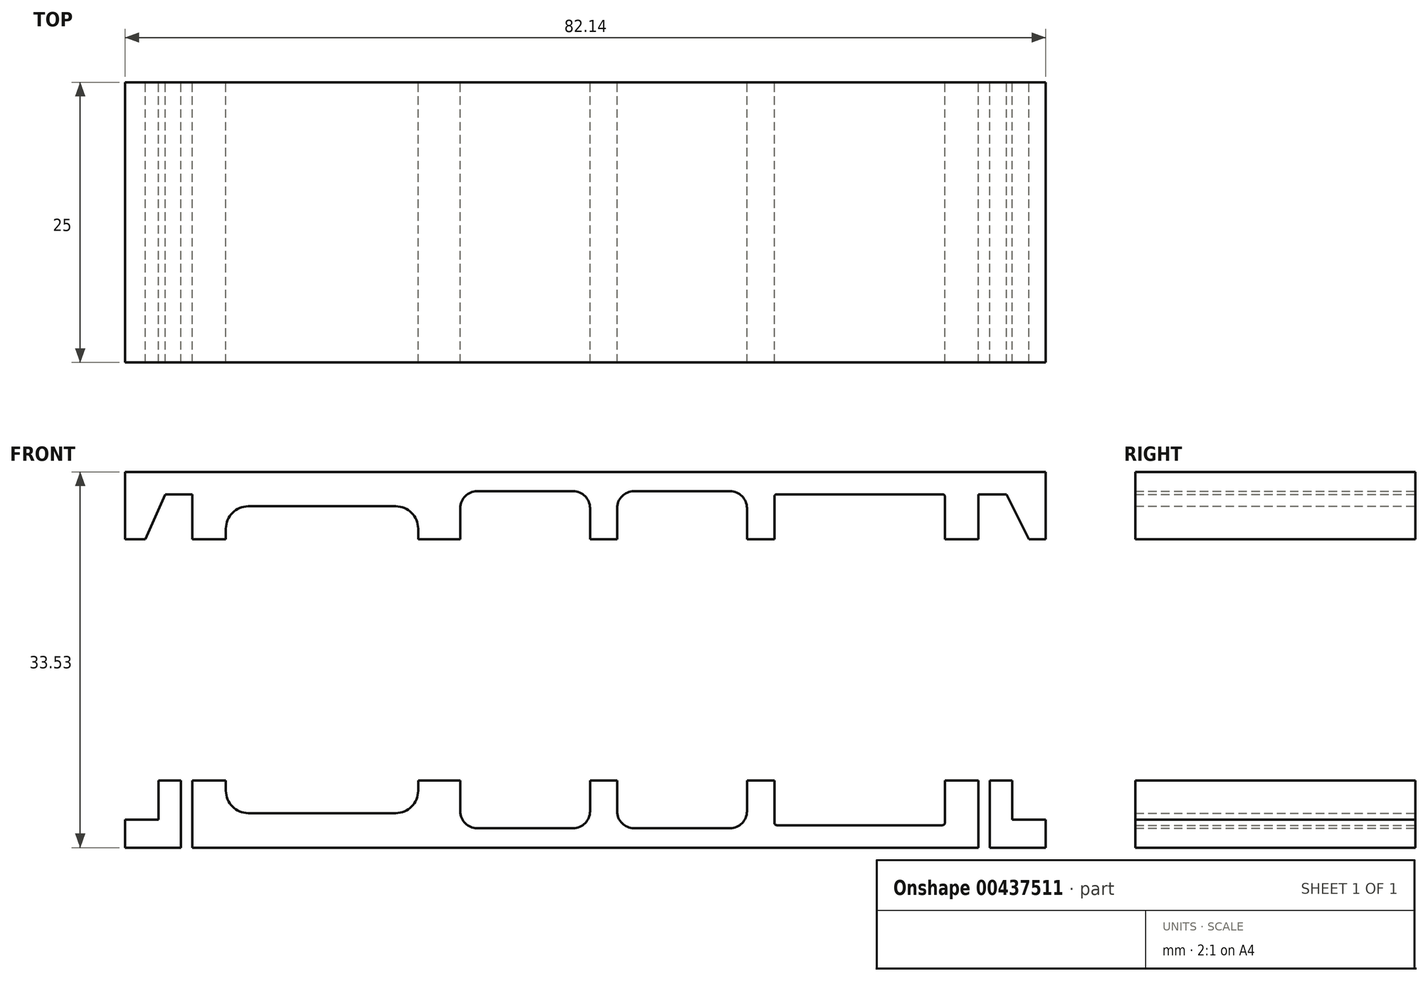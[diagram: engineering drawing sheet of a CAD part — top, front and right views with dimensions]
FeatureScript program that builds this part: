
annotation { "Feature Type Name" : "Feature", "Feature Type Description" : "" }
export const myFeature = defineFeature(function(context is Context, id is Id, definition is map)
    precondition{}
    {
        {
            var Q0;
            Q0=qCreatedBy(makeId("Front.planeOp"),FACE);
            var sketch = newSketch(context, id + "F0", { "sketchPlane" : qUnion([Q0])});
            skLineSegment(sketch, "E0.bottom", {"start": v(33.57, -6) * mm, "end": v(-33.57, -6) * mm});
            skLineSegment(sketch, "E0.top", {"start": v(33.57, 6) * mm, "end": v(-33.57, 6) * mm});
            skLineSegment(sketch, "E0.left", {"start": v(35.07, -4.5) * mm, "end": v(35.07, 4.5) * mm});
            skLineSegment(sketch, "E0.right", {"start": v(-35.07, -4.5) * mm, "end": v(-35.07, 4.5) * mm});
            skPoint(sketch, "E0.middle", {"position": v(0, 0) * mm});
            skLineSegment(sketch, "E1", {"start": v(-35.07, 0) * mm, "end": v(35.07, 0) * mm, "construction": true});
            skLineSegment(sketch, "E2.bottom", {"start": v(-16.92, -2.92) * mm, "end": v(-30.07, -2.92) * mm});
            skLineSegment(sketch, "E2.top", {"start": v(-16.92, 2.93) * mm, "end": v(-30.07, 2.93) * mm});
            skLineSegment(sketch, "E2.left", {"start": v(-14.92, -0.92) * mm, "end": v(-14.92, 0.93) * mm});
            skLineSegment(sketch, "E2.right", {"start": v(-32.07, -0.92) * mm, "end": v(-32.07, 0.93) * mm});
            skPoint(sketch, "E2.middle", {"position": v(-23.5, 0) * mm});
            skLineSegment(sketch, "E3.bottom", {"start": v(-1.09, 4.27) * mm, "end": v(-9.67, 4.27) * mm});
            skLineSegment(sketch, "E3.top", {"start": v(-1.09, -4.26) * mm, "end": v(-9.67, -4.26) * mm});
            skLineSegment(sketch, "E3.left", {"start": v(0.41, 2.77) * mm, "end": v(0.41, -2.76) * mm});
            skLineSegment(sketch, "E3.right", {"start": v(-11.17, 2.77) * mm, "end": v(-11.17, -2.76) * mm});
            skPoint(sketch, "E3.middle", {"position": v(-5.38, 0) * mm});
            skLineSegment(sketch, "E4.bottom", {"start": v(12.91, 4.27) * mm, "end": v(4.33, 4.27) * mm});
            skLineSegment(sketch, "E4.top", {"start": v(12.91, -4.26) * mm, "end": v(4.33, -4.26) * mm});
            skLineSegment(sketch, "E4.left", {"start": v(14.41, 2.77) * mm, "end": v(14.41, -2.76) * mm});
            skLineSegment(sketch, "E4.right", {"start": v(2.83, 2.77) * mm, "end": v(2.83, -2.76) * mm});
            skPoint(sketch, "E4.middle", {"position": v(8.62, 0) * mm});
            skLineSegment(sketch, "E5.bottom", {"start": v(31.87, -4) * mm, "end": v(17.07, -4) * mm});
            skLineSegment(sketch, "E5.top", {"start": v(31.87, 4) * mm, "end": v(17.07, 4) * mm});
            skLineSegment(sketch, "E5.left", {"start": v(32.07, -3.8) * mm, "end": v(32.07, 3.8) * mm});
            skLineSegment(sketch, "E5.right", {"start": v(16.87, -3.8) * mm, "end": v(16.87, 3.8) * mm});
            skPoint(sketch, "E5.middle", {"position": v(24.47, 0) * mm});
            skPoint(sketch, "E6.visualSharp", {"position": v(-32.07, 2.93) * mm});
            skArc(sketch, "E6.filletArc", {"start": v(-30.07, 2.93) * mm, "mid": v(-31.49, 2.34) * mm, "end": v(-32.07, 0.93) * mm});
            skPoint(sketch, "E7.visualSharp", {"position": v(-14.92, 2.93) * mm});
            skArc(sketch, "E7.filletArc", {"start": v(-14.92, 0.93) * mm, "mid": v(-15.5, 2.34) * mm, "end": v(-16.92, 2.93) * mm});
            skPoint(sketch, "E8.visualSharp", {"position": v(-14.92, -2.92) * mm});
            skArc(sketch, "E8.filletArc", {"start": v(-16.92, -2.92) * mm, "mid": v(-15.5, -2.34) * mm, "end": v(-14.92, -0.92) * mm});
            skPoint(sketch, "E9.visualSharp", {"position": v(-32.07, -2.93) * mm});
            skArc(sketch, "E9.filletArc", {"start": v(-32.07, -0.92) * mm, "mid": v(-31.49, -2.34) * mm, "end": v(-30.07, -2.92) * mm});
            skPoint(sketch, "E10.visualSharp", {"position": v(-11.17, 4.27) * mm});
            skArc(sketch, "E10.filletArc", {"start": v(-9.67, 4.27) * mm, "mid": v(-10.73, 3.83) * mm, "end": v(-11.17, 2.77) * mm});
            skPoint(sketch, "E11.visualSharp", {"position": v(0.41, 4.27) * mm});
            skArc(sketch, "E11.filletArc", {"start": v(0.41, 2.77) * mm, "mid": v(-0.03, 3.83) * mm, "end": v(-1.09, 4.27) * mm});
            skPoint(sketch, "E12.visualSharp", {"position": v(-11.17, -4.26) * mm});
            skArc(sketch, "E12.filletArc", {"start": v(-11.17, -2.76) * mm, "mid": v(-10.73, -3.83) * mm, "end": v(-9.67, -4.26) * mm});
            skPoint(sketch, "E13.visualSharp", {"position": v(0.41, -4.26) * mm});
            skArc(sketch, "E13.filletArc", {"start": v(-1.09, -4.26) * mm, "mid": v(-0.03, -3.83) * mm, "end": v(0.41, -2.76) * mm});
            skPoint(sketch, "E14.visualSharp", {"position": v(2.83, 4.26) * mm});
            skArc(sketch, "E14.filletArc", {"start": v(4.33, 4.26) * mm, "mid": v(3.27, 3.83) * mm, "end": v(2.83, 2.77) * mm});
            skPoint(sketch, "E15.visualSharp", {"position": v(14.41, 4.27) * mm});
            skArc(sketch, "E15.filletArc", {"start": v(14.41, 2.77) * mm, "mid": v(13.97, 3.83) * mm, "end": v(12.91, 4.27) * mm});
            skPoint(sketch, "E16.visualSharp", {"position": v(14.41, -4.26) * mm});
            skArc(sketch, "E16.filletArc", {"start": v(12.91, -4.26) * mm, "mid": v(13.97, -3.83) * mm, "end": v(14.41, -2.76) * mm});
            skPoint(sketch, "E17.visualSharp", {"position": v(2.83, -4.26) * mm});
            skArc(sketch, "E17.filletArc", {"start": v(2.83, -2.76) * mm, "mid": v(3.27, -3.83) * mm, "end": v(4.33, -4.26) * mm});
            skPoint(sketch, "E18.visualSharp", {"position": v(16.87, 4) * mm});
            skArc(sketch, "E18.filletArc", {"start": v(17.07, 4) * mm, "mid": v(16.93, 3.94) * mm, "end": v(16.87, 3.8) * mm});
            skPoint(sketch, "E19.visualSharp", {"position": v(32.07, 4) * mm});
            skArc(sketch, "E19.filletArc", {"start": v(32.07, 3.8) * mm, "mid": v(32.01, 3.94) * mm, "end": v(31.87, 4) * mm});
            skPoint(sketch, "E20.visualSharp", {"position": v(32.07, -4) * mm});
            skArc(sketch, "E20.filletArc", {"start": v(31.87, -4) * mm, "mid": v(32.01, -3.94) * mm, "end": v(32.07, -3.8) * mm});
            skPoint(sketch, "E21.visualSharp", {"position": v(16.87, -4) * mm});
            skArc(sketch, "E21.filletArc", {"start": v(16.87, -3.8) * mm, "mid": v(16.93, -3.94) * mm, "end": v(17.07, -4) * mm});
            skPoint(sketch, "E22.visualSharp", {"position": v(-35.07, 6) * mm});
            skPoint(sketch, "E23.visualSharp", {"position": v(35.07, -6) * mm});
            skPoint(sketch, "E24.visualSharp", {"position": v(-35.07, -6) * mm});
            skLineSegment(sketch, "E25", {"start": v(-35.07, 0) * mm, "end": v(35.07, 0) * mm});
            skLineSegment(sketch, "E26.bottom", {"start": v(-35.07, 6) * mm, "end": v(35.07, 6) * mm});
            skLineSegment(sketch, "E26.top", {"start": v(-35.07, -6) * mm, "end": v(35.07, -6) * mm});
            skLineSegment(sketch, "E26.left", {"start": v(-35.07, 6) * mm, "end": v(-35.07, -6) * mm});
            skLineSegment(sketch, "E26.right", {"start": v(35.07, 6) * mm, "end": v(35.07, -6) * mm});
            skLineSegment(sketch, "E27.bottom", {"start": v(35.07, 6) * mm, "end": v(41.07, 6) * mm});
            skLineSegment(sketch, "E27.top", {"start": v(35.07, -6) * mm, "end": v(41.07, -6) * mm});
            skLineSegment(sketch, "E27.right", {"start": v(41.07, 6) * mm, "end": v(41.07, -6) * mm});
            skLineSegment(sketch, "E28.bottom", {"start": v(-35.07, 6) * mm, "end": v(-41.07, 6) * mm});
            skLineSegment(sketch, "E28.top", {"start": v(-35.07, -6) * mm, "end": v(-41.07, -6) * mm});
            skLineSegment(sketch, "E28.right", {"start": v(-41.07, 6) * mm, "end": v(-41.07, -6) * mm});
            skLineSegment(sketch, "E29.bottom", {"start": v(33.57, -27.53) * mm, "end": v(-33.57, -27.53) * mm});
            skLineSegment(sketch, "E29.top", {"start": v(33.57, -15.53) * mm, "end": v(-33.57, -15.53) * mm});
            skLineSegment(sketch, "E29.left", {"start": v(35.07, -26.03) * mm, "end": v(35.07, -17.03) * mm});
            skLineSegment(sketch, "E29.right", {"start": v(-35.07, -26.03) * mm, "end": v(-35.07, -17.03) * mm});
            skPoint(sketch, "E29.middle", {"position": v(0, -21.53) * mm});
            skLineSegment(sketch, "E30", {"start": v(-35.07, -21.53) * mm, "end": v(35.07, -21.53) * mm, "construction": true});
            skLineSegment(sketch, "E31.bottom", {"start": v(-16.92, -24.45) * mm, "end": v(-30.07, -24.45) * mm});
            skLineSegment(sketch, "E31.top", {"start": v(-16.92, -18.6) * mm, "end": v(-30.07, -18.6) * mm});
            skLineSegment(sketch, "E31.left", {"start": v(-14.92, -22.45) * mm, "end": v(-14.92, -20.6) * mm});
            skLineSegment(sketch, "E31.right", {"start": v(-32.07, -22.45) * mm, "end": v(-32.07, -20.6) * mm});
            skPoint(sketch, "E31.middle", {"position": v(-23.5, -21.53) * mm});
            skLineSegment(sketch, "E32.bottom", {"start": v(-1.09, -17.26) * mm, "end": v(-9.67, -17.26) * mm});
            skLineSegment(sketch, "E32.top", {"start": v(-1.09, -25.8) * mm, "end": v(-9.67, -25.8) * mm});
            skLineSegment(sketch, "E32.left", {"start": v(0.41, -18.76) * mm, "end": v(0.41, -24.3) * mm});
            skLineSegment(sketch, "E32.right", {"start": v(-11.17, -18.76) * mm, "end": v(-11.17, -24.3) * mm});
            skPoint(sketch, "E32.middle", {"position": v(-5.38, -21.53) * mm});
            skLineSegment(sketch, "E33.bottom", {"start": v(12.91, -17.26) * mm, "end": v(4.33, -17.26) * mm});
            skLineSegment(sketch, "E33.top", {"start": v(12.91, -25.8) * mm, "end": v(4.33, -25.8) * mm});
            skLineSegment(sketch, "E33.left", {"start": v(14.41, -18.76) * mm, "end": v(14.41, -24.3) * mm});
            skLineSegment(sketch, "E33.right", {"start": v(2.83, -18.76) * mm, "end": v(2.83, -24.3) * mm});
            skPoint(sketch, "E33.middle", {"position": v(8.62, -21.53) * mm});
            skLineSegment(sketch, "E34.bottom", {"start": v(31.87, -25.53) * mm, "end": v(17.07, -25.53) * mm});
            skLineSegment(sketch, "E34.top", {"start": v(31.87, -17.53) * mm, "end": v(17.07, -17.53) * mm});
            skLineSegment(sketch, "E34.left", {"start": v(32.07, -25.33) * mm, "end": v(32.07, -17.73) * mm});
            skLineSegment(sketch, "E34.right", {"start": v(16.87, -25.33) * mm, "end": v(16.87, -17.73) * mm});
            skPoint(sketch, "E34.middle", {"position": v(24.47, -21.53) * mm});
            skPoint(sketch, "E35.visualSharp", {"position": v(-32.07, -18.6) * mm});
            skArc(sketch, "E35.filletArc", {"start": v(-30.07, -18.6) * mm, "mid": v(-31.49, -19.19) * mm, "end": v(-32.07, -20.6) * mm});
            skPoint(sketch, "E36.visualSharp", {"position": v(-14.92, -18.6) * mm});
            skArc(sketch, "E36.filletArc", {"start": v(-14.92, -20.6) * mm, "mid": v(-15.5, -19.19) * mm, "end": v(-16.92, -18.6) * mm});
            skPoint(sketch, "E37.visualSharp", {"position": v(-14.92, -24.45) * mm});
            skArc(sketch, "E37.filletArc", {"start": v(-16.92, -24.45) * mm, "mid": v(-15.5, -23.87) * mm, "end": v(-14.92, -22.45) * mm});
            skPoint(sketch, "E38.visualSharp", {"position": v(-32.07, -24.45) * mm});
            skArc(sketch, "E38.filletArc", {"start": v(-32.07, -22.45) * mm, "mid": v(-31.49, -23.87) * mm, "end": v(-30.07, -24.45) * mm});
            skPoint(sketch, "E39.visualSharp", {"position": v(-11.17, -17.26) * mm});
            skArc(sketch, "E39.filletArc", {"start": v(-9.67, -17.26) * mm, "mid": v(-10.73, -17.7) * mm, "end": v(-11.17, -18.76) * mm});
            skPoint(sketch, "E40.visualSharp", {"position": v(0.41, -17.26) * mm});
            skArc(sketch, "E40.filletArc", {"start": v(0.41, -18.76) * mm, "mid": v(-0.03, -17.7) * mm, "end": v(-1.09, -17.26) * mm});
            skPoint(sketch, "E41.visualSharp", {"position": v(-11.17, -25.8) * mm});
            skArc(sketch, "E41.filletArc", {"start": v(-11.17, -24.3) * mm, "mid": v(-10.73, -25.35) * mm, "end": v(-9.67, -25.8) * mm});
            skPoint(sketch, "E42.visualSharp", {"position": v(0.41, -25.8) * mm});
            skArc(sketch, "E42.filletArc", {"start": v(-1.09, -25.8) * mm, "mid": v(-0.03, -25.35) * mm, "end": v(0.41, -24.3) * mm});
            skPoint(sketch, "E43.visualSharp", {"position": v(2.83, -17.26) * mm});
            skArc(sketch, "E43.filletArc", {"start": v(4.33, -17.26) * mm, "mid": v(3.27, -17.7) * mm, "end": v(2.83, -18.76) * mm});
            skPoint(sketch, "E44.visualSharp", {"position": v(14.41, -17.26) * mm});
            skArc(sketch, "E44.filletArc", {"start": v(14.41, -18.76) * mm, "mid": v(13.97, -17.7) * mm, "end": v(12.91, -17.26) * mm});
            skPoint(sketch, "E45.visualSharp", {"position": v(14.41, -25.8) * mm});
            skArc(sketch, "E45.filletArc", {"start": v(12.91, -25.8) * mm, "mid": v(13.97, -25.35) * mm, "end": v(14.41, -24.3) * mm});
            skPoint(sketch, "E46.visualSharp", {"position": v(2.83, -25.8) * mm});
            skArc(sketch, "E46.filletArc", {"start": v(2.83, -24.3) * mm, "mid": v(3.27, -25.35) * mm, "end": v(4.33, -25.8) * mm});
            skPoint(sketch, "E47.visualSharp", {"position": v(16.87, -17.53) * mm});
            skArc(sketch, "E47.filletArc", {"start": v(17.07, -17.53) * mm, "mid": v(16.93, -17.59) * mm, "end": v(16.87, -17.73) * mm});
            skPoint(sketch, "E48.visualSharp", {"position": v(32.07, -17.53) * mm});
            skArc(sketch, "E48.filletArc", {"start": v(32.07, -17.73) * mm, "mid": v(32.01, -17.59) * mm, "end": v(31.87, -17.53) * mm});
            skPoint(sketch, "E49.visualSharp", {"position": v(32.07, -25.53) * mm});
            skArc(sketch, "E49.filletArc", {"start": v(31.87, -25.53) * mm, "mid": v(32.01, -25.47) * mm, "end": v(32.07, -25.33) * mm});
            skPoint(sketch, "E50.visualSharp", {"position": v(16.87, -25.53) * mm});
            skArc(sketch, "E50.filletArc", {"start": v(16.87, -25.33) * mm, "mid": v(16.93, -25.47) * mm, "end": v(17.07, -25.53) * mm});
            skPoint(sketch, "E51.visualSharp", {"position": v(-35.07, -15.53) * mm});
            skPoint(sketch, "E52.visualSharp", {"position": v(35.07, -15.53) * mm});
            skPoint(sketch, "E53.visualSharp", {"position": v(35.07, -27.53) * mm});
            skPoint(sketch, "E54.visualSharp", {"position": v(-35.07, -27.53) * mm});
            skLineSegment(sketch, "E55", {"start": v(-35.07, -21.53) * mm, "end": v(35.07, -21.53) * mm});
            skLineSegment(sketch, "E56.bottom", {"start": v(-35.07, -15.53) * mm, "end": v(35.07, -15.53) * mm});
            skLineSegment(sketch, "E56.top", {"start": v(-35.07, -27.53) * mm, "end": v(35.07, -27.53) * mm});
            skLineSegment(sketch, "E56.left", {"start": v(-35.07, -15.53) * mm, "end": v(-35.07, -27.53) * mm});
            skLineSegment(sketch, "E56.right", {"start": v(35.07, -15.53) * mm, "end": v(35.07, -27.53) * mm});
            skLineSegment(sketch, "E57.bottom", {"start": v(35.07, -15.53) * mm, "end": v(41.07, -15.53) * mm});
            skLineSegment(sketch, "E57.top", {"start": v(35.07, -27.53) * mm, "end": v(41.07, -27.53) * mm});
            skLineSegment(sketch, "E57.right", {"start": v(41.07, -15.53) * mm, "end": v(41.07, -27.53) * mm});
            skLineSegment(sketch, "E58.bottom", {"start": v(-35.07, -15.53) * mm, "end": v(-41.07, -15.53) * mm});
            skLineSegment(sketch, "E58.top", {"start": v(-35.07, -27.53) * mm, "end": v(-41.07, -27.53) * mm});
            skLineSegment(sketch, "E58.right", {"start": v(-41.07, -15.53) * mm, "end": v(-41.07, -27.53) * mm});
            skLineSegment(sketch, "E59", {"start": v(35.07, 0) * mm, "end": v(41.07, 0) * mm});
            skLineSegment(sketch, "E60", {"start": v(41.07, -6) * mm, "end": v(38.07, 0) * mm});
            skLineSegment(sketch, "E61", {"start": v(38.07, 0) * mm, "end": v(39.57, 0) * mm});
            skLineSegment(sketch, "E62", {"start": v(35.07, -21.53) * mm, "end": v(41.07, -21.53) * mm});
            skLineSegment(sketch, "E63", {"start": v(41.07, -27.53) * mm, "end": v(38.07, -21.53) * mm});
            skLineSegment(sketch, "E64", {"start": v(38.07, -21.53) * mm, "end": v(39.07, -21.53) * mm});
            skLineSegment(sketch, "E65", {"start": v(39.07, -21.53) * mm, "end": v(35.07, -15.53) * mm});
            skLineSegment(sketch, "E66", {"start": v(36.07, -27.53) * mm, "end": v(36.07, -17.03) * mm});
            skLineSegment(sketch, "E67", {"start": v(38.07, -21.53) * mm, "end": v(38.07, -27.53) * mm});
            skLineSegment(sketch, "E68", {"start": v(35.07, -3) * mm, "end": v(41.07, -3) * mm});
            skLineSegment(sketch, "E69", {"start": v(41.07, -25.03) * mm, "end": v(35.07, -25.03) * mm});
            skLineSegment(sketch, "E70", {"start": v(39.57, 0) * mm, "end": v(36.57, 6) * mm});
            skLineSegment(sketch, "E71", {"start": v(37.07, -18.53) * mm, "end": v(36.07, -18.53) * mm});
            skLineSegment(sketch, "E72", {"start": v(35.07, 4) * mm, "end": v(37.57, 4) * mm});
            skLineSegment(sketch, "E73", {"start": v(-35.07, 0) * mm, "end": v(-41.07, 0) * mm});
            skLineSegment(sketch, "E74", {"start": v(-35.07, -21.53) * mm, "end": v(-41.07, -21.53) * mm});
            skLineSegment(sketch, "E75", {"start": v(-41.07, -27.53) * mm, "end": v(-38.07, -21.53) * mm});
            skLineSegment(sketch, "E76", {"start": v(-38.07, -21.53) * mm, "end": v(-39.07, -21.53) * mm});
            skLineSegment(sketch, "E77", {"start": v(-39.07, -21.53) * mm, "end": v(-38.07, -21.53) * mm});
            skLineSegment(sketch, "E78", {"start": v(-39.07, -21.53) * mm, "end": v(-35.07, -15.53) * mm});
            skLineSegment(sketch, "E79", {"start": v(-36.07, -27.53) * mm, "end": v(-36.07, -17.03) * mm});
            skLineSegment(sketch, "E80", {"start": v(-36.07, -18.53) * mm, "end": v(-37.07, -18.53) * mm});
            skLineSegment(sketch, "E81", {"start": v(-38.07, -21.53) * mm, "end": v(-38.07, -27.53) * mm});
            skLineSegment(sketch, "E82", {"start": v(-41.07, -6) * mm, "end": v(-38.07, 0) * mm});
            skLineSegment(sketch, "E83", {"start": v(-38.07, 0) * mm, "end": v(-39.27, 0) * mm});
            skLineSegment(sketch, "E84", {"start": v(-39.27, 0) * mm, "end": v(-36.57, 6) * mm});
            skLineSegment(sketch, "E85", {"start": v(-36.57, 6) * mm, "end": v(-35.07, 6) * mm});
            skLineSegment(sketch, "E86", {"start": v(-37.47, 4) * mm, "end": v(-35.07, 4) * mm});
            skLineSegment(sketch, "E87", {"start": v(-41.07, -3) * mm, "end": v(-35.07, -3) * mm});
            skLineSegment(sketch, "E88", {"start": v(-35.07, -25.03) * mm, "end": v(-41.07, -25.03) * mm});
            skLineSegment(sketch, "E89.bottom", {"start": v(-41.07, 6) * mm, "end": v(41.07, 6) * mm});
            skLineSegment(sketch, "E89.top", {"start": v(-41.07, 9) * mm, "end": v(41.07, 9) * mm});
            skLineSegment(sketch, "E89.left", {"start": v(-41.07, 6) * mm, "end": v(-41.07, 9) * mm});
            skLineSegment(sketch, "E89.right", {"start": v(41.07, 6) * mm, "end": v(41.07, 9) * mm});
            skSolve(sketch);
        }
        {
            var Q0;
            {var subQ0=sQuery(id+"F0.wireOp",EDGE,"E89.bottom");var subQ1=sQuery(id+"F0.wireOp",EDGE,"E84");var subQ2=makeQuery(id+"F0.imprint","INTERSECT",VERTEX,{"derivedFrom":[subQ1,subQ0]});Q0=makeQuery(id+"F0.imprint","IMPRINT",FACE,{"disambiguationData":[TD([[makeQuery(id+"F0.imprint","IMPRINT",EDGE,{"disambiguationData":[TD([[subQ2,1.0]])],"derivedFrom":subQ1}),1.0]])]});}
            var Q1;
            {var subQ0=sQuery(id+"F0.wireOp",EDGE,"E86");Q1=makeQuery(id+"F0.imprint","IMPRINT",FACE,{"disambiguationData":[TD([[makeQuery(id+"F0.imprint","IMPRINT",EDGE,{"derivedFrom":subQ0}),1.0]])]});}
            var Q2;
            Q2=makeQuery(id+"F0.imprint","IMPRINT",FACE,{"disambiguationData":[TD([[makeQuery(id+"F0.imprint","IMPRINT",EDGE,{"derivedFrom":sQuery(id+"F0.wireOp",EDGE,"E2.top")}),-1.0]])]});
            var Q3;
            {var subQ0=sQuery(id+"F0.wireOp",EDGE,"E72");Q3=makeQuery(id+"F0.imprint","IMPRINT",FACE,{"disambiguationData":[TD([[makeQuery(id+"F0.imprint","IMPRINT",EDGE,{"derivedFrom":subQ0}),1.0]])]});}
            var Q4;
            {var subQ0=sQuery(id+"F0.wireOp",EDGE,"E89.bottom");var subQ1=sQuery(id+"F0.wireOp",EDGE,"E70");var subQ2=makeQuery(id+"F0.imprint","INTERSECT",VERTEX,{"derivedFrom":[subQ1,subQ0]});Q4=makeQuery(id+"F0.imprint","IMPRINT",FACE,{"disambiguationData":[TD([[makeQuery(id+"F0.imprint","IMPRINT",EDGE,{"disambiguationData":[TD([[subQ2,1.0]])],"derivedFrom":subQ1}),-1.0]])]});}
            var Q5;
            {var subQ0=sQuery(id+"F0.wireOp",EDGE,"E61");Q5=makeQuery(id+"F0.imprint","IMPRINT",FACE,{"disambiguationData":[TD([[makeQuery(id+"F0.imprint","IMPRINT",EDGE,{"derivedFrom":subQ0}),-1.0]])]});}
            var Q6;
            {var subQ0=sQuery(id+"F0.wireOp",EDGE,"E83");Q6=makeQuery(id+"F0.imprint","IMPRINT",FACE,{"disambiguationData":[TD([[makeQuery(id+"F0.imprint","IMPRINT",EDGE,{"derivedFrom":subQ0}),1.0]])]});}
            extrude(context, id + "F1", {"entities" : qUnion([Q0, Q1, Q2, Q3, Q4, Q5, Q6]), "depth" : 25 * mm});
        }
        {
            var Q0;
            {var subQ0=sQuery(id+"F0.wireOp",EDGE,"E77");Q0=makeQuery(id+"F0.imprint","IMPRINT",FACE,{"disambiguationData":[TD([[makeQuery(id+"F0.imprint","IMPRINT",EDGE,{"derivedFrom":subQ0}),1.0]])]});}
            var Q1;
            {var subQ1=sQuery(id+"F0.wireOp",EDGE,"E74");var subQ3=sQuery(id+"F0.wireOp",EDGE,"E79");var subQ4=makeQuery(id+"F0.imprint","INTERSECT",VERTEX,{"derivedFrom":[subQ1,subQ3]});Q1=makeQuery(id+"F0.imprint","IMPRINT",FACE,{"disambiguationData":[TD([[makeQuery(id+"F0.imprint","IMPRINT",EDGE,{"disambiguationData":[TD([[subQ4,1.0]])],"derivedFrom":subQ3}),1.0]])]});}
            var Q2;
            {var subQ0=sQuery(id+"F0.wireOp",EDGE,"E79");var subQ1=sQuery(id+"F0.wireOp",EDGE,"E58.top");var subQ2=makeQuery(id+"F0.imprint","INTERSECT",VERTEX,{"derivedFrom":[subQ1,subQ0]});Q2=makeQuery(id+"F0.imprint","IMPRINT",FACE,{"disambiguationData":[TD([[makeQuery(id+"F0.imprint","IMPRINT",EDGE,{"disambiguationData":[TD([[subQ2,-1.0]])],"derivedFrom":subQ1}),-1.0]])]});}
            var Q3;
            {var subQ1=sQuery(id+"F0.wireOp",EDGE,"E58.top");var subQ3=sQuery(id+"F0.wireOp",EDGE,"E81");var subQ4=makeQuery(id+"F0.imprint","INTERSECT",VERTEX,{"derivedFrom":[subQ1,subQ3]});Q3=makeQuery(id+"F0.imprint","IMPRINT",FACE,{"disambiguationData":[TD([[makeQuery(id+"F0.imprint","IMPRINT",EDGE,{"disambiguationData":[TD([[subQ4,1.0]])],"derivedFrom":subQ3}),-1.0]])]});}
            var Q4;
            {var subQ1=sQuery(id+"F0.wireOp",EDGE,"E58.right");var subQ3=sQuery(id+"F0.wireOp",EDGE,"E88");var subQ4=makeQuery(id+"F0.imprint","INTERSECT",VERTEX,{"derivedFrom":[subQ1,subQ3]});Q4=makeQuery(id+"F0.imprint","IMPRINT",FACE,{"disambiguationData":[TD([[makeQuery(id+"F0.imprint","IMPRINT",EDGE,{"disambiguationData":[TD([[subQ4,1.0]])],"derivedFrom":subQ3}),1.0]])]});}
            var Q5;
            {var subQ5=sQuery(id+"F0.wireOp",EDGE,"E56.left");var subQ7=makeQuery(id+"F0.imprint","IMPRINT",VERTEX,{"disambiguationData":[OD(1.0)],"derivedFrom":subQ5});Q5=makeQuery(id+"F0.imprint","IMPRINT",FACE,{"disambiguationData":[TD([[makeQuery(id+"F0.imprint","IMPRINT",EDGE,{"disambiguationData":[TD([[subQ7,1.0]])],"derivedFrom":subQ5}),-1.0]])]});}
            var Q6;
            Q6=makeQuery(id+"F0.imprint","IMPRINT",FACE,{"disambiguationData":[TD([[makeQuery(id+"F0.imprint","IMPRINT",EDGE,{"derivedFrom":sQuery(id+"F0.wireOp",EDGE,"E31.bottom")}),1.0]])]});
            var Q7;
            {var subQ5=sQuery(id+"F0.wireOp",EDGE,"E56.right");var subQ8=makeQuery(id+"F0.imprint","IMPRINT",VERTEX,{"disambiguationData":[OD(1.0)],"derivedFrom":subQ5});Q7=makeQuery(id+"F0.imprint","IMPRINT",FACE,{"disambiguationData":[TD([[makeQuery(id+"F0.imprint","IMPRINT",EDGE,{"disambiguationData":[TD([[subQ8,1.0]])],"derivedFrom":subQ5}),1.0]])]});}
            var Q8;
            {var subQ0=sQuery(id+"F0.wireOp",EDGE,"E66");var subQ1=sQuery(id+"F0.wireOp",EDGE,"E57.top");var subQ2=makeQuery(id+"F0.imprint","INTERSECT",VERTEX,{"derivedFrom":[subQ1,subQ0]});Q8=makeQuery(id+"F0.imprint","IMPRINT",FACE,{"disambiguationData":[TD([[makeQuery(id+"F0.imprint","IMPRINT",EDGE,{"disambiguationData":[TD([[subQ2,-1.0]])],"derivedFrom":subQ1}),1.0]])]});}
            var Q9;
            {var subQ1=sQuery(id+"F0.wireOp",EDGE,"E57.top");var subQ3=sQuery(id+"F0.wireOp",EDGE,"E67");var subQ4=makeQuery(id+"F0.imprint","INTERSECT",VERTEX,{"derivedFrom":[subQ1,subQ3]});Q9=makeQuery(id+"F0.imprint","IMPRINT",FACE,{"disambiguationData":[TD([[makeQuery(id+"F0.imprint","IMPRINT",EDGE,{"disambiguationData":[TD([[subQ4,1.0]])],"derivedFrom":subQ3}),1.0]])]});}
            var Q10;
            {var subQ1=sQuery(id+"F0.wireOp",EDGE,"E57.right");var subQ3=sQuery(id+"F0.wireOp",EDGE,"E69");var subQ4=makeQuery(id+"F0.imprint","INTERSECT",VERTEX,{"derivedFrom":[subQ1,subQ3]});Q10=makeQuery(id+"F0.imprint","IMPRINT",FACE,{"disambiguationData":[TD([[makeQuery(id+"F0.imprint","IMPRINT",EDGE,{"disambiguationData":[TD([[subQ4,-1.0]])],"derivedFrom":subQ3}),1.0]])]});}
            var Q11;
            {var subQ1=sQuery(id+"F0.wireOp",EDGE,"E62");var subQ3=sQuery(id+"F0.wireOp",EDGE,"E66");var subQ4=makeQuery(id+"F0.imprint","INTERSECT",VERTEX,{"derivedFrom":[subQ1,subQ3]});Q11=makeQuery(id+"F0.imprint","IMPRINT",FACE,{"disambiguationData":[TD([[makeQuery(id+"F0.imprint","IMPRINT",EDGE,{"disambiguationData":[TD([[subQ4,1.0]])],"derivedFrom":subQ3}),-1.0]])]});}
            var Q12;
            {var subQ0=sQuery(id+"F0.wireOp",EDGE,"E64");Q12=makeQuery(id+"F0.imprint","IMPRINT",FACE,{"disambiguationData":[TD([[makeQuery(id+"F0.imprint","IMPRINT",EDGE,{"derivedFrom":subQ0}),1.0]])]});}
            extrude(context, id + "F2", {"entities" : qUnion([Q0, Q1, Q2, Q3, Q4, Q5, Q6, Q7, Q8, Q9, Q10, Q11, Q12]), "depth" : 25 * mm});
        }
    });
